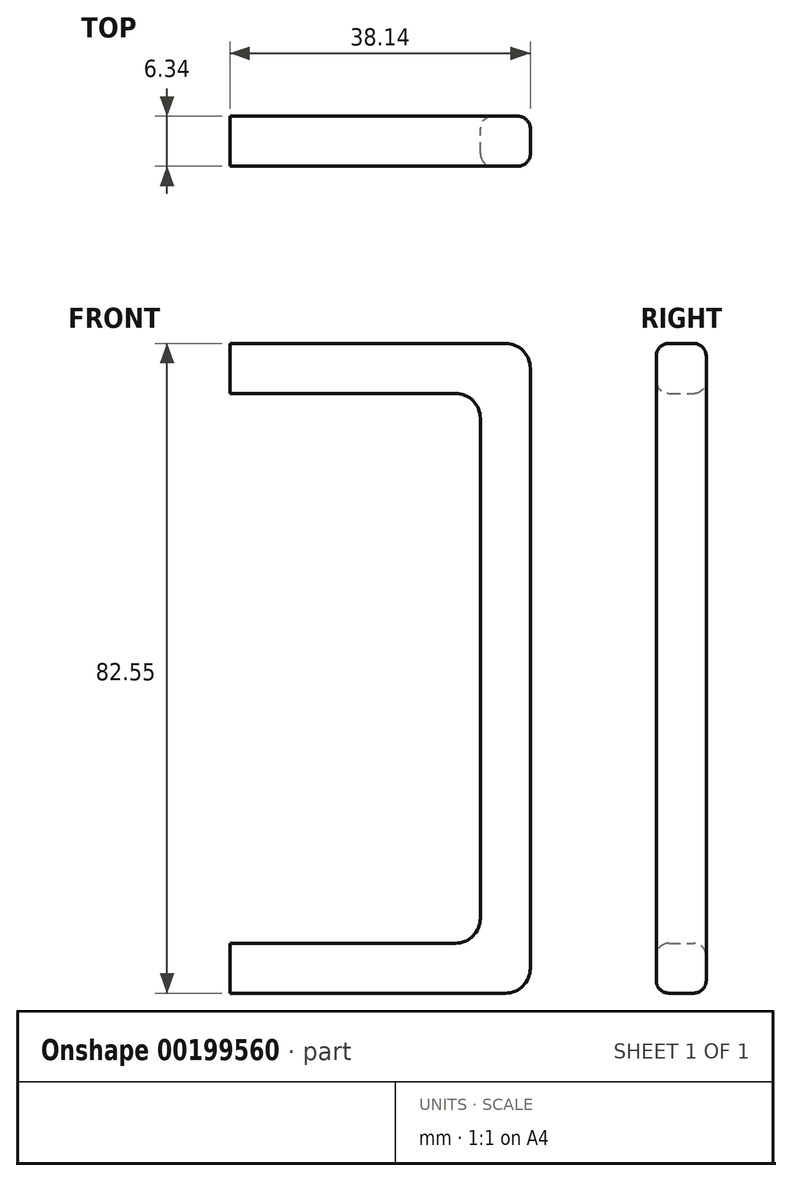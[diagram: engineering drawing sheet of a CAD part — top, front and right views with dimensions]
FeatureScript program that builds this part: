
annotation { "Feature Type Name" : "Feature", "Feature Type Description" : "" }
export const myFeature = defineFeature(function(context is Context, id is Id, definition is map)
    precondition{}
    {
        {
            var Q0;
            Q0=qCreatedBy(makeId("Front.planeOp"),FACE);
            var sketch = newSketch(context, id + "F0", { "sketchPlane" : qUnion([Q0])});
            skLineSegment(sketch, "E0", {"start": v(0, 0) * mm, "end": v(0, 107.95) * mm, "construction": true});
            skLineSegment(sketch, "E1", {"start": v(0, 107.95) * mm, "end": v(38.1, 107.95) * mm});
            skLineSegment(sketch, "E2", {"start": v(41.28, 104.78) * mm, "end": v(41.28, 3.17) * mm});
            skLineSegment(sketch, "E3", {"start": v(38.1, 0) * mm, "end": v(0, 0) * mm});
            skPoint(sketch, "E4.visualSharp", {"position": v(41.28, 0) * mm});
            skArc(sketch, "E4.filletArc", {"start": v(38.1, 0) * mm, "mid": v(40.35, 0.93) * mm, "end": v(41.28, 3.18) * mm});
            skPoint(sketch, "E5.visualSharp", {"position": v(41.28, 107.95) * mm});
            skArc(sketch, "E5.filletArc", {"start": v(41.28, 104.78) * mm, "mid": v(40.35, 107.02) * mm, "end": v(38.1, 107.95) * mm});
            skSolve(sketch);
        }
        {
            var Q0;
            Q0=sQuery(id+"F0.wireOp",EDGE,"E2");
            var Q1;
            Q1=sQuery(id+"F0.wireOp",EDGE,"E3");
            var Q2;
            Q2=sQuery(id+"F0.wireOp",EDGE,"E5.filletArc");
            var Q3;
            Q3=sQuery(id+"F0.wireOp",EDGE,"E4.filletArc");
            var Q4;
            Q4=sQuery(id+"F0.wireOp",EDGE,"E0");
            revolve(context, id + "F1", {"bodyType" : ToolBodyType.SURFACE, "surfaceEntities" : qUnion([Q0, Q1, Q2, Q3]), "axis" : qUnion([Q4]), "revolveType" : RevolveType.FULL});
        }
        {
            var Q0;
            Q0=qCreatedBy(makeId("Front.planeOp"),FACE);
            var sketch = newSketch(context, id + "F2", { "sketchPlane" : qUnion([Q0])});
            skLineSegment(sketch, "E6.bottom", {"start": v(37.4, 95.25) * mm, "end": v(72.37, 95.25) * mm});
            skLineSegment(sketch, "E6.top", {"start": v(37.4, 12.7) * mm, "end": v(72.37, 12.7) * mm});
            skLineSegment(sketch, "E6.left", {"start": v(37.4, 95.25) * mm, "end": v(37.4, 88.9) * mm});
            skLineSegment(sketch, "E6.right", {"start": v(75.54, 92.08) * mm, "end": v(75.54, 15.88) * mm});
            skLineSegment(sketch, "E7.0", {"start": v(37.4, 19.05) * mm, "end": v(66.02, 19.05) * mm});
            skLineSegment(sketch, "E7.1", {"start": v(69.2, 85.73) * mm, "end": v(69.2, 22.23) * mm});
            skLineSegment(sketch, "E7.2", {"start": v(37.4, 88.9) * mm, "end": v(66.02, 88.9) * mm});
            skLineSegment(sketch, "E8.trimOffspring", {"start": v(37.4, 19.05) * mm, "end": v(37.4, 12.7) * mm});
            skPoint(sketch, "E9.visualSharp", {"position": v(69.2, 88.9) * mm});
            skArc(sketch, "E9.filletArc", {"start": v(69.2, 85.73) * mm, "mid": v(68.26, 87.97) * mm, "end": v(66.02, 88.9) * mm});
            skPoint(sketch, "E10.visualSharp", {"position": v(75.54, 95.25) * mm});
            skArc(sketch, "E10.filletArc", {"start": v(75.54, 92.08) * mm, "mid": v(74.61, 94.32) * mm, "end": v(72.37, 95.25) * mm});
            skPoint(sketch, "E11.visualSharp", {"position": v(69.2, 19.05) * mm});
            skArc(sketch, "E11.filletArc", {"start": v(66.02, 19.05) * mm, "mid": v(68.26, 19.98) * mm, "end": v(69.2, 22.23) * mm});
            skPoint(sketch, "E12.visualSharp", {"position": v(75.54, 12.7) * mm});
            skArc(sketch, "E12.filletArc", {"start": v(72.37, 12.7) * mm, "mid": v(74.61, 13.63) * mm, "end": v(75.54, 15.88) * mm});
            skSolve(sketch);
        }
        {
            var Q0;
            Q0 = qSketchRegion(id + "F2", true);
            extrude(context, id + "F3", {"entities" : qUnion([Q0]), "endBound" : BoundingType.SYMMETRIC, "depth" : 6.35 * mm});
        }
        {
            var Q0;
            Q0=makeQuery(id+"F3.opExtrude","CAP_EDGE",EDGE,{"disambiguationData":[OSD([sQuery(id+"F2.wireOp",EDGE,"E6.top")])],"isStart":false});
            var Q1;
            Q1=makeQuery(id+"F3.opExtrude","CAP_EDGE",EDGE,{"disambiguationData":[OSD([sQuery(id+"F2.wireOp",EDGE,"E6.top")])],"isStart":true});
            var Q2;
            Q2=makeQuery(id+"F3.opExtrude","CAP_EDGE",EDGE,{"disambiguationData":[OSD([sQuery(id+"F2.wireOp",EDGE,"E7.0")])],"isStart":true});
            var Q3;
            Q3=makeQuery(id+"F3.opExtrude","CAP_EDGE",EDGE,{"disambiguationData":[OSD([sQuery(id+"F2.wireOp",EDGE,"E7.0")])],"isStart":false});
            fillet(context, id + "F4", {"entities" : qUnion([Q0, Q1, Q2, Q3]), "radius" : 1.59 * mm, "tangentPropagation" : true, "allowEdgeOverflow" : false});
        }
    });
